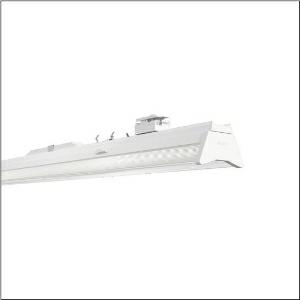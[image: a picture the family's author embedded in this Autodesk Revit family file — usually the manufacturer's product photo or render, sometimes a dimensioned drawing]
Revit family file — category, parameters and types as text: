
# Revit family: licross_r__21_performance_mo_52tm16cn36xg_705a
name_source: partatom
category: Lighting Fixtures
units: mm (PartAtom-declared; Revit-internal decimal feet)

## family parameters
Cut with Voids When Loaded = No
Host = Face
Light Source = No
Part Type = Normal
Room Calculation Point = No
Round Connector Dimension = Use Diameter
Shared = No

## types (1)
- --- (1 x LED, 6000 lm, 34.1 W, 3000K)
    Apparent Load = 34 VA
    CIE Flux Codes = 66 88 96 79 100
    Color Rendering = 80
    Color Temperature = 3000K
    Default Elevation = 1800 mm
    Description = Licross® 21 Performance MO, luminaire insert, of sheet steel, galvanised, coil coated, white, length: 1.500mm, width: 120mm, height: 123mm, LED rated luminous flux: 6.000lm, light colour: 830, control gear: ON/OFF Multilumen, CLOi, control gear: ECG Multilumen, with plug, 3-pole, with phase selection, mains connection: 220..240V, AC, 50/60Hz, start of lifetime: 34W, end of service life: 40W, internal wiring halogen-free, primary light control with lens, of plastic, primary optical cover: cover, of PMMA, light emission: direct/indirect distribution, primary light characteristic: symmetric, protection rating (complete): IP40, insulation class (complete): insulation class I (protective earthing), certification: CE, ENEC, UKCA, protection symbol: D if used in an environment without relevant dust loads with corresponding accessories, impact resistance: IK06, permissible ambient temperature for indoor applications: -25..+55°C, corresponds to IFS (International Featured Standards) requirements for safety and quality in the food industry, reducing of maximum allowable ambient temperature of 5°C with ceiling mounting, LABS conformity tested according to VDMA 24364:2018-05, packaging unit: 1 piece
    Height = 114 mm
    Lamp = 1 x LED
    Lamp Light Flux = 6000 lm
    Lamp Power = 34.1 W
    Lamp count = 1
    Length = 1500 mm
    Luminous efficacy = 176 lm/W
    Manufacturer = Siteco
    ModVariant = No
    Model = 52TM16CN36XG
    Mounting Place = Ceiling
    Mounting Type = Pendant
    Number of Poles = 1
    OnlyDefault = Yes
    Power Factor = 1
    Product Name = Licross® 21 Performance MO
    Product group = luminaire insert | ceiling pendant
    ProductGroupID = 902
    Protection Class = Protection class I
    Protection Degree = IP 40
    RLX_Detail_Level = 1
    RLX_Emergency_Light_Flux = 0 lm
    RLX_Emergency_Type = 0
    RLX_Emergency_Type_DB = No
    RlxData = <blob elided: 31761 chars, md5=b5186165>
    Socket = socket
    Standby Power = 0 W
    System Light Flux = 6000 lm
    System Power = 34 W
    Type Comments = factory setting: luminous flux: 100 % | (A | C | E) | 79 mA
    Type Image = l_1256138.jpg
    URL = http://relux.com
    VarID = @adj_018863
    Voltage = 0 V
    Weight = 0.00 kg
    Width = 120 mm

## geometry (parser evidence)
native form markers: Blend x4, Sweep x13
no freeform markers — native parametric forms only
